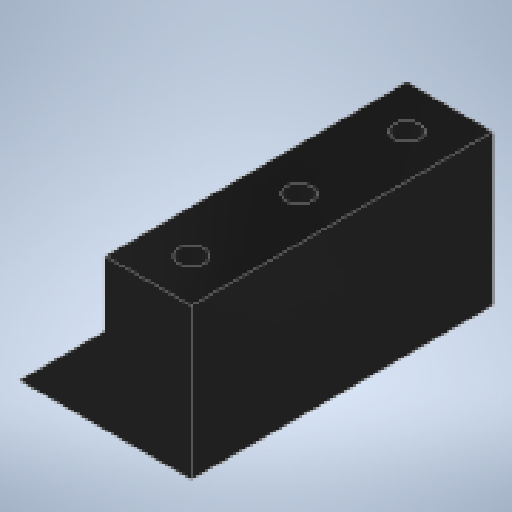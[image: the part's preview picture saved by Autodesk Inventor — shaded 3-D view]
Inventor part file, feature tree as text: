
AUTODESK INVENTOR PART (.ipt)
format: ipt  version: 2025.1 (Build 291241020, 241B)  size: 371,200 bytes
history: native  units: mm
features: sketch x3, extrude x2, hole x1
ambient origin geometry x8: Origin, YZ Plane, XZ Plane, XY Plane, X Axis, Y Axis, Z Axis, Center Point
bodies: Solid1 (feature_tree)
feature tree (6):
  extrude  "Extrusion1"  Depth=20.0mm
  hole  "Hole1"  [1 undecoded]
  extrude  "Extrusion2"  Depth=10.0mm
  sketch  "Sketch1"  dims[d0=70.0mm d1=20.0mm]
  sketch  "Sketch2"  dims[d2=35.0mm d3=0.0mm d5=10.0mm]
  sketch  "Sketch3"  dims[d6=10.0mm d7=6.0mm d8=6.0mm d9=4.0mm d10=2.0mm d11=90.0deg d12=8.0mm d13=20.594885mm d14=25.0mm d15=25.0mm d16=20.0mm d17=45.0deg d18=10.0mm d19=0.0mm]
note: 1 required parameter value undecoded (feature->parameter linkage not recoverable at this tier; creation-order binding heuristic only, values carry confidence <= 0.55)
